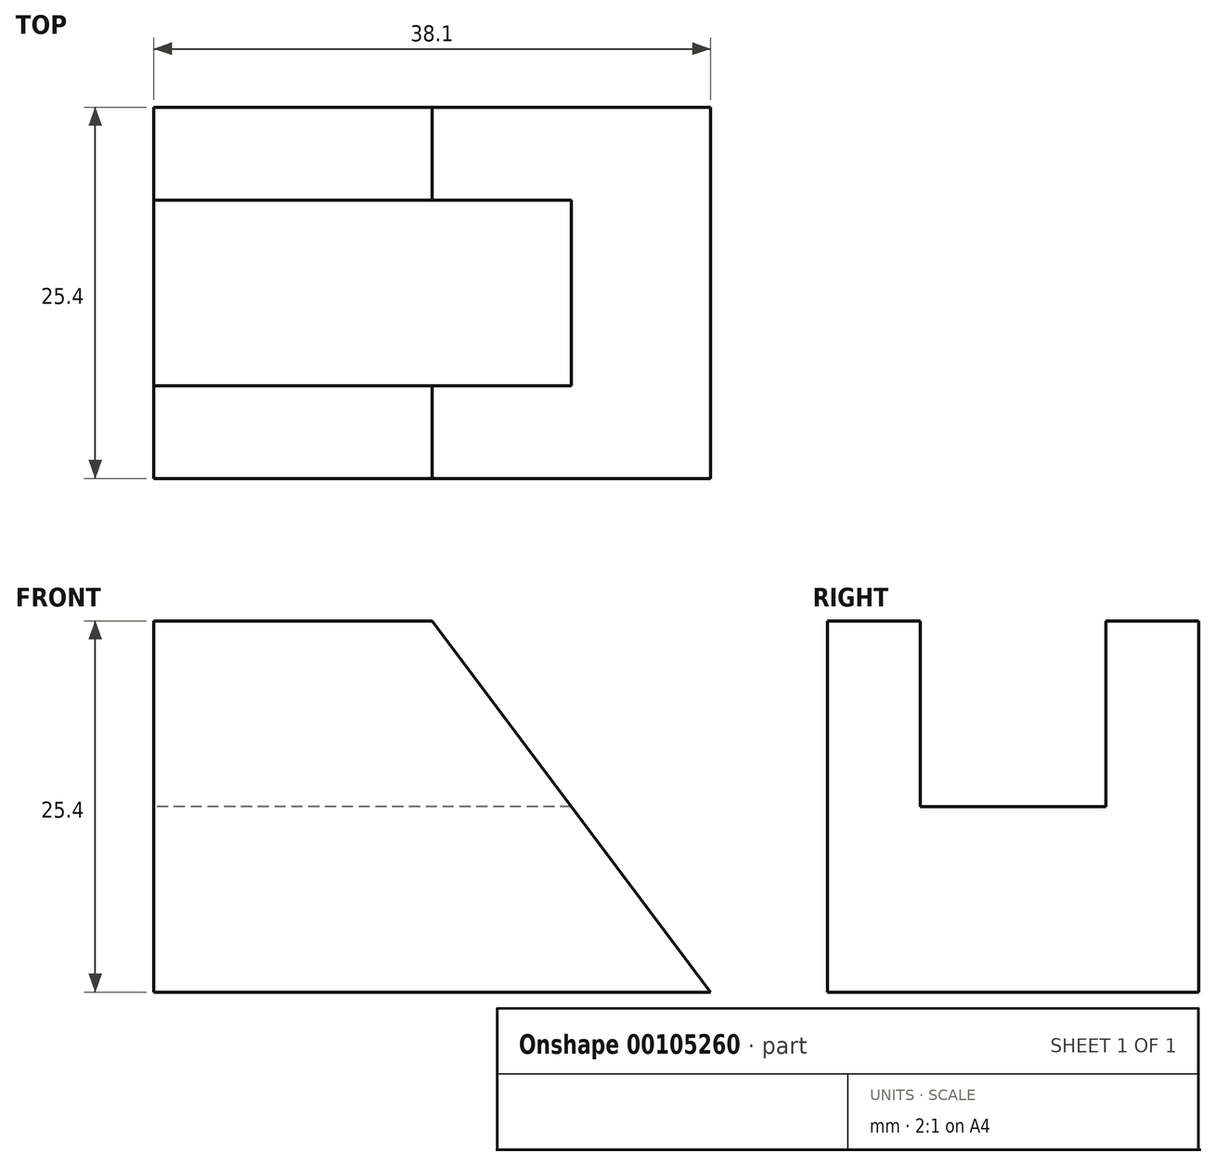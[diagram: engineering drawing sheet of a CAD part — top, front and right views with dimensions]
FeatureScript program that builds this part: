
annotation { "Feature Type Name" : "Feature", "Feature Type Description" : "" }
export const myFeature = defineFeature(function(context is Context, id is Id, definition is map)
    precondition{}
    {
        {
            var Q0;
            Q0=qCreatedBy(makeId("Front.planeOp"),FACE);
            var sketch = newSketch(context, id + "F0", { "sketchPlane" : qUnion([Q0])});
            skLineSegment(sketch, "E0", {"start": v(0, 0) * mm, "end": v(0, 25.4) * mm});
            skLineSegment(sketch, "E1", {"start": v(0, 25.4) * mm, "end": v(19.05, 25.4) * mm});
            skLineSegment(sketch, "E2", {"start": v(19.05, 25.4) * mm, "end": v(38.1, 0) * mm});
            skLineSegment(sketch, "E3", {"start": v(38.1, 0) * mm, "end": v(0, 0) * mm});
            skSolve(sketch);
        }
        {
            var Q0;
            Q0 = qSketchRegion(id + "F0", true);
            extrude(context, id + "F1", {"entities" : qUnion([Q0]), "depth" : 25.4 * mm});
        }
        {
            var Q0;
            Q0=qCreatedBy(makeId("Right.planeOp"),FACE);
            var sketch = newSketch(context, id + "F2", { "sketchPlane" : qUnion([Q0])});
            skLineSegment(sketch, "E4.bottom", {"start": v(-19.05, 25.4) * mm, "end": v(-6.35, 25.4) * mm});
            skLineSegment(sketch, "E4.top", {"start": v(-19.05, 12.7) * mm, "end": v(-6.35, 12.7) * mm});
            skLineSegment(sketch, "E4.left", {"start": v(-19.05, 25.4) * mm, "end": v(-19.05, 12.7) * mm});
            skLineSegment(sketch, "E4.right", {"start": v(-6.35, 25.4) * mm, "end": v(-6.35, 12.7) * mm});
            skSolve(sketch);
        }
        {
            var Q0;
            Q0 = qSketchRegion(id + "F2", true);
            extrude(context, id + "F3", {"entities" : qUnion([Q0]), "operationType" : NewBodyOperationType.REMOVE, "depth" : 38.1 * mm});
        }
    });
